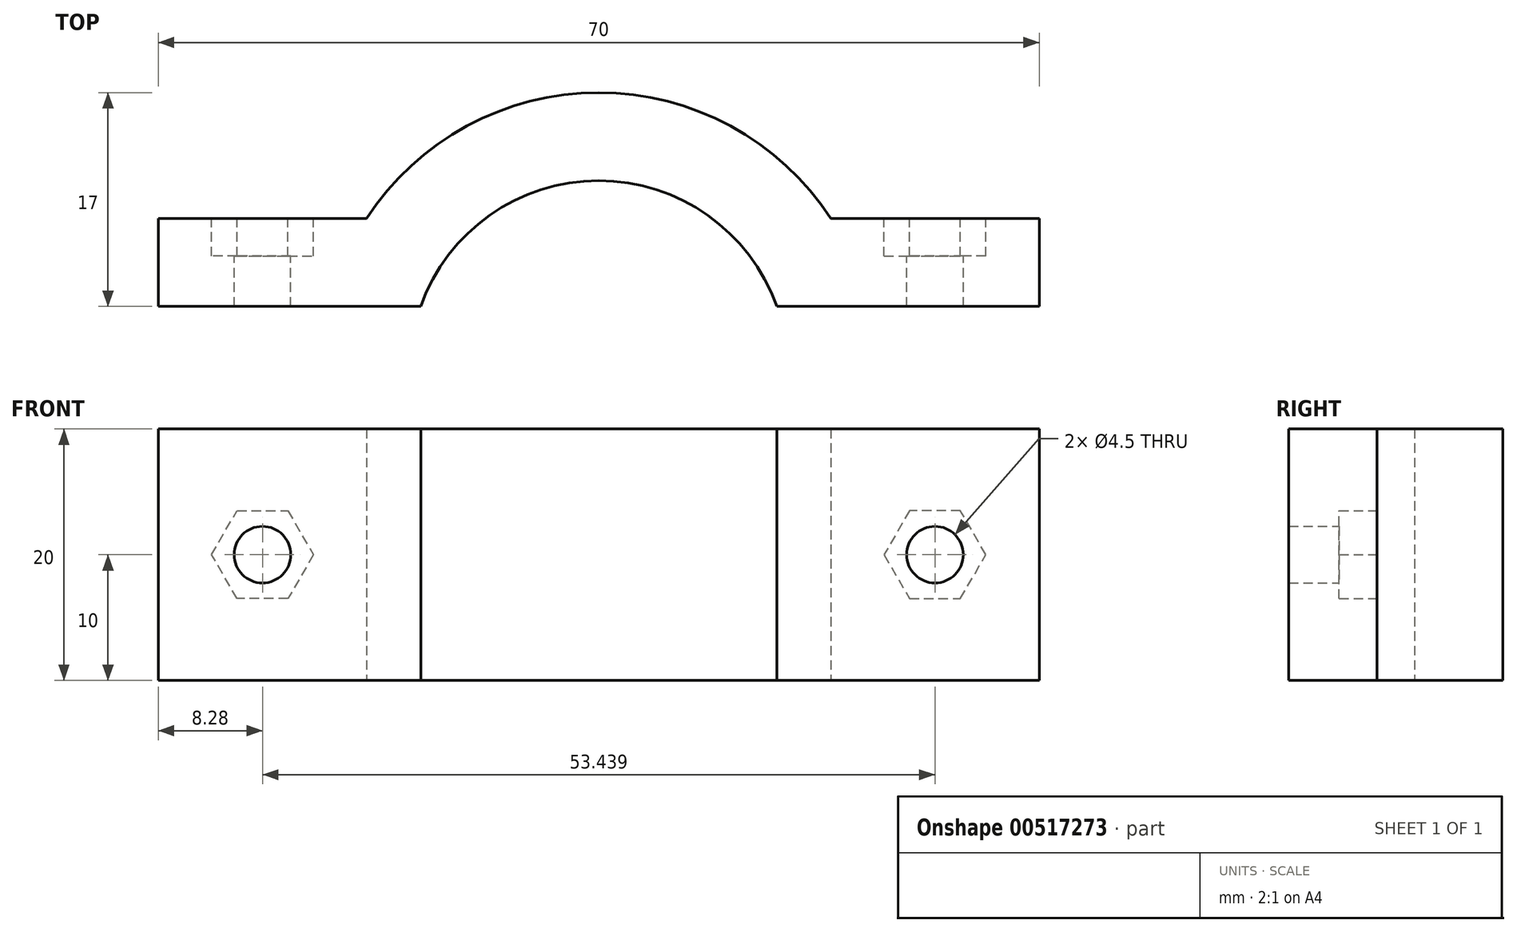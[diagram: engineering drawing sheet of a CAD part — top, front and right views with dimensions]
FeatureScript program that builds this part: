
annotation { "Feature Type Name" : "Feature", "Feature Type Description" : "" }
export const myFeature = defineFeature(function(context is Context, id is Id, definition is map)
    precondition{}
    {
        {
            var Q0;
            Q0=qCreatedBy(makeId("Top.planeOp"),FACE);
            var sketch = newSketch(context, id + "F0", { "sketchPlane" : qUnion([Q0])});
            skLineSegment(sketch, "E0", {"start": v(-35, 0) * mm, "end": v(-14.14, 0) * mm});
            skLineSegment(sketch, "E1.MirrorCS", {"start": v(35, 0) * mm, "end": v(14.14, 0) * mm});
            skArc(sketch, "E2", {"start": v(14.14, 0) * mm, "mid": v(0, 10) * mm, "end": v(-14.14, 0) * mm});
            skArc(sketch, "E3.0", {"start": v(18.44, 7) * mm, "mid": v(0, 17) * mm, "end": v(-18.44, 7) * mm});
            skLineSegment(sketch, "E4.0", {"start": v(-35, 7) * mm, "end": v(-18.44, 7) * mm});
            skLineSegment(sketch, "E5.MirrorCS", {"start": v(35, 7) * mm, "end": v(18.44, 7) * mm});
            skLineSegment(sketch, "E6.MirrorCS", {"start": v(35, 7) * mm, "end": v(35, 0) * mm});
            skLineSegment(sketch, "E7", {"start": v(-35, 7) * mm, "end": v(-35, 0) * mm});
            skSolve(sketch);
        }
        {
            var Q0;
            Q0 = qSketchRegion(id + "F0", true);
            extrude(context, id + "F1", {"entities" : qUnion([Q0]), "endBound" : BoundingType.SYMMETRIC, "depth" : 20 * mm, "offsetDistance" : 25 * mm});
        }
        {
            var Q0;
            Q0=makeQuery(id+"F1.opExtrude","SWEPT_FACE",FACE,{"disambiguationData":[OSD([sQuery(id+"F0.wireOp",EDGE,"E5.MirrorCS")])]});
            var sketch = newSketch(context, id + "F2", { "sketchPlane" : qUnion([Q0])});
            skCircle(sketch, "E8", {"center": v(-26.72, 0) * mm, "radius": 2.25 * mm});
            skLineSegment(sketch, "E9", {"start": v(-26.72, 10) * mm, "end": v(-26.72, -10) * mm, "construction": true});
            skCircle(sketch, "E10.MirrorC", {"center": v(26.72, 0) * mm, "radius": 2.25 * mm});
            skSolve(sketch);
        }
        {
            var Q0;
            Q0 = qSketchRegion(id + "F2", true);
            extrude(context, id + "F3", {"entities" : qUnion([Q0]), "operationType" : NewBodyOperationType.REMOVE, "oppositeDirection" : true, "depth" : 25 * mm, "offsetDistance" : 25 * mm});
        }
        {
            var Q0;
            Q0=makeQuery(id+"F1.opExtrude","SWEPT_FACE",FACE,{"disambiguationData":[OSD([sQuery(id+"F0.wireOp",EDGE,"E5.MirrorCS")])]});
            var sketch = newSketch(context, id + "F4", { "sketchPlane" : qUnion([Q0])});
            skCircle(sketch, "E11.0", {"center": v(-26.72, 0) * mm, "radius": 2.25 * mm});
            skCircle(sketch, "E12.cCircle", {"center": v(-26.72, 0) * mm, "radius": 3.5 * mm, "construction": true});
            skLineSegment(sketch, "E12.0", {"start": v(-30.76, 0) * mm, "end": v(-28.74, 3.5) * mm});
            skLineSegment(sketch, "E12.1", {"start": v(-28.74, 3.5) * mm, "end": v(-24.7, 3.5) * mm});
            skLineSegment(sketch, "E12.2", {"start": v(-24.7, 3.5) * mm, "end": v(-22.68, 0) * mm});
            skLineSegment(sketch, "E12.3", {"start": v(-22.68, 0) * mm, "end": v(-24.7, -3.5) * mm});
            skLineSegment(sketch, "E12.4", {"start": v(-24.7, -3.5) * mm, "end": v(-28.74, -3.5) * mm});
            skLineSegment(sketch, "E12.5", {"start": v(-28.74, -3.5) * mm, "end": v(-30.76, 0) * mm});
            skPoint(sketch, "E12.0.midPoint", {"position": v(-29.75, 1.75) * mm});
            skLineSegment(sketch, "E13.MirrorCS", {"start": v(30.76, 0) * mm, "end": v(28.74, 3.5) * mm});
            skLineSegment(sketch, "E14.MirrorCS", {"start": v(28.74, 3.5) * mm, "end": v(24.7, 3.5) * mm});
            skLineSegment(sketch, "E15.MirrorCS", {"start": v(24.7, 3.5) * mm, "end": v(22.68, 0) * mm});
            skLineSegment(sketch, "E16.MirrorCS", {"start": v(22.68, 0) * mm, "end": v(24.7, -3.5) * mm});
            skPoint(sketch, "E17.MirrorP", {"position": v(29.75, 1.75) * mm});
            skCircle(sketch, "E18.MirrorC", {"center": v(26.72, 0) * mm, "radius": 3.5 * mm, "construction": true});
            skLineSegment(sketch, "E19.MirrorCS", {"start": v(24.7, -3.5) * mm, "end": v(28.74, -3.5) * mm});
            skLineSegment(sketch, "E20.MirrorCS", {"start": v(28.74, -3.5) * mm, "end": v(30.76, 0) * mm});
            skSolve(sketch);
        }
        {
            var Q0;
            Q0 = qSketchRegion(id + "F4", true);
            extrude(context, id + "F5", {"entities" : qUnion([Q0]), "operationType" : NewBodyOperationType.REMOVE, "oppositeDirection" : true, "depth" : 3 * mm, "offsetDistance" : 25 * mm});
        }
    });
